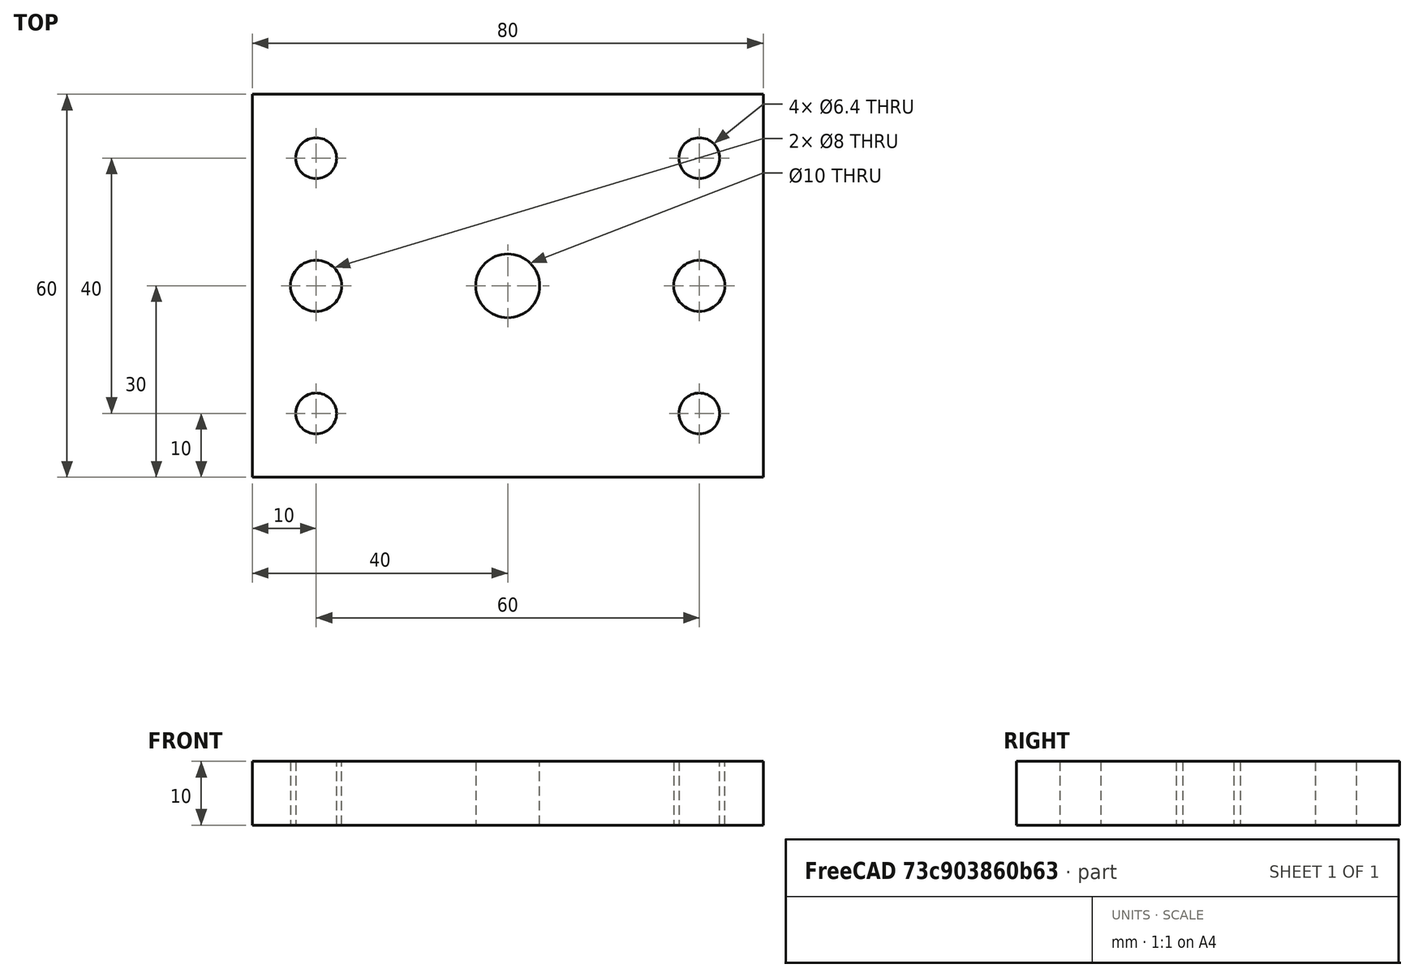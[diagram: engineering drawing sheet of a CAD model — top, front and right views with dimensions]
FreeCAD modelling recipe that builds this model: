
FCSTD DOCUMENT  (FreeCAD 0.18R16110 (Git))
Label: mountplate1c_loslager
License: All rights reserved
LicenseURL: http://en.wikipedia.org/wiki/All_rights_reserved
objects: Sketcher::SketchObject×1, PartDesign::Pad×1, PartDesign::Body×1
note: 4 computed .brp shape members not serialized (recipe doc carries the construction recipe); baked Part::Feature solids carry a one-line shape summary decoded from their .brp

FEATURE [Sketcher::SketchObject] Sketch
  MapMode = 5
  Support = -> [XY_Plane]
  sketch-geometry (11):
    g0: LineSegment StartX=0 StartY=60 StartZ=0 EndX=80 EndY=60 EndZ=0
    g1: LineSegment StartX=80 StartY=60 StartZ=0 EndX=80 EndY=0 EndZ=0
    g2: LineSegment StartX=80 StartY=0 StartZ=0 EndX=0 EndY=0 EndZ=0
    g3: LineSegment StartX=0 StartY=0 StartZ=0 EndX=0 EndY=60 EndZ=0
    g4: Circle CenterX=40 CenterY=30 CenterZ=0 NormalX=0 NormalY=0 NormalZ=1 AngleXU=0 Radius=5
    g5: Circle CenterX=10 CenterY=10 CenterZ=0 NormalX=0 NormalY=0 NormalZ=1 AngleXU=0 Radius=3.2
    g6: Circle CenterX=70 CenterY=10 CenterZ=0 NormalX=0 NormalY=0 NormalZ=1 AngleXU=0 Radius=3.2
    g7: Circle CenterX=70 CenterY=30 CenterZ=0 NormalX=0 NormalY=0 NormalZ=1 AngleXU=0 Radius=4
    g8: Circle CenterX=10 CenterY=30 CenterZ=0 NormalX=0 NormalY=0 NormalZ=1 AngleXU=0 Radius=4
    g9: Circle CenterX=10 CenterY=50 CenterZ=0 NormalX=0 NormalY=0 NormalZ=1 AngleXU=0 Radius=3.2
    g10: Circle CenterX=70 CenterY=50 CenterZ=0 NormalX=0 NormalY=0 NormalZ=1 AngleXU=0 Radius=3.2
  constraints (32):
    c: Coincident(g0,g1)
    c: Coincident(g1,g2)
    c: Coincident(g2,g3)
    c: Coincident(g3,g0)
    c: Horizontal(g0)
    c: Horizontal(g2)
    c: Vertical(g1)
    c: Vertical(g3)
    c: Coincident(g2,g-1)
    c: DistanceY(g3,g3) = 60
    c: DistanceX(g2,g2) = 80
    c: DistanceX(g2,g4) = 40
    c: DistanceY(g2,g4) = 30
    c: Radius(g4) = 5
    c: DistanceX(g2,g5) = 10
    c: DistanceY(g2,g5) = 10
    c: DistanceY(g5,g6) = 0
    c: DistanceX(g6,g1) = 10
    c: DistanceX(g8,g5) = 0
    c: DistanceY(g7,g8) = 0
    c: DistanceX(g7,g0) = 10
    c: DistanceY(g8,g0) = 30
    c: Radius(g5) = 3.2
    c: Equal(g5,g6)
    c: Radius(g8) = 4
    c: Equal(g8,g7)
    c: DistanceX(g7,g10) = 0
    c: DistanceX(g9,g8) = 0
    c: DistanceY(g9,g0) = 10
    c: DistanceY(g10,g0) = 10
    c: Radius(g10) = 3.2
    c: Radius(g9) = 3.2
FEATURE [PartDesign::Pad] Pad
  Length = 10
  Length2 = 100
  Profile = -> Sketch
  Type = 0
FEATURE [PartDesign::Body] Body
  Group = -> [Sketch,Pad]
  Origin = -> Origin
  Tip = -> Pad
